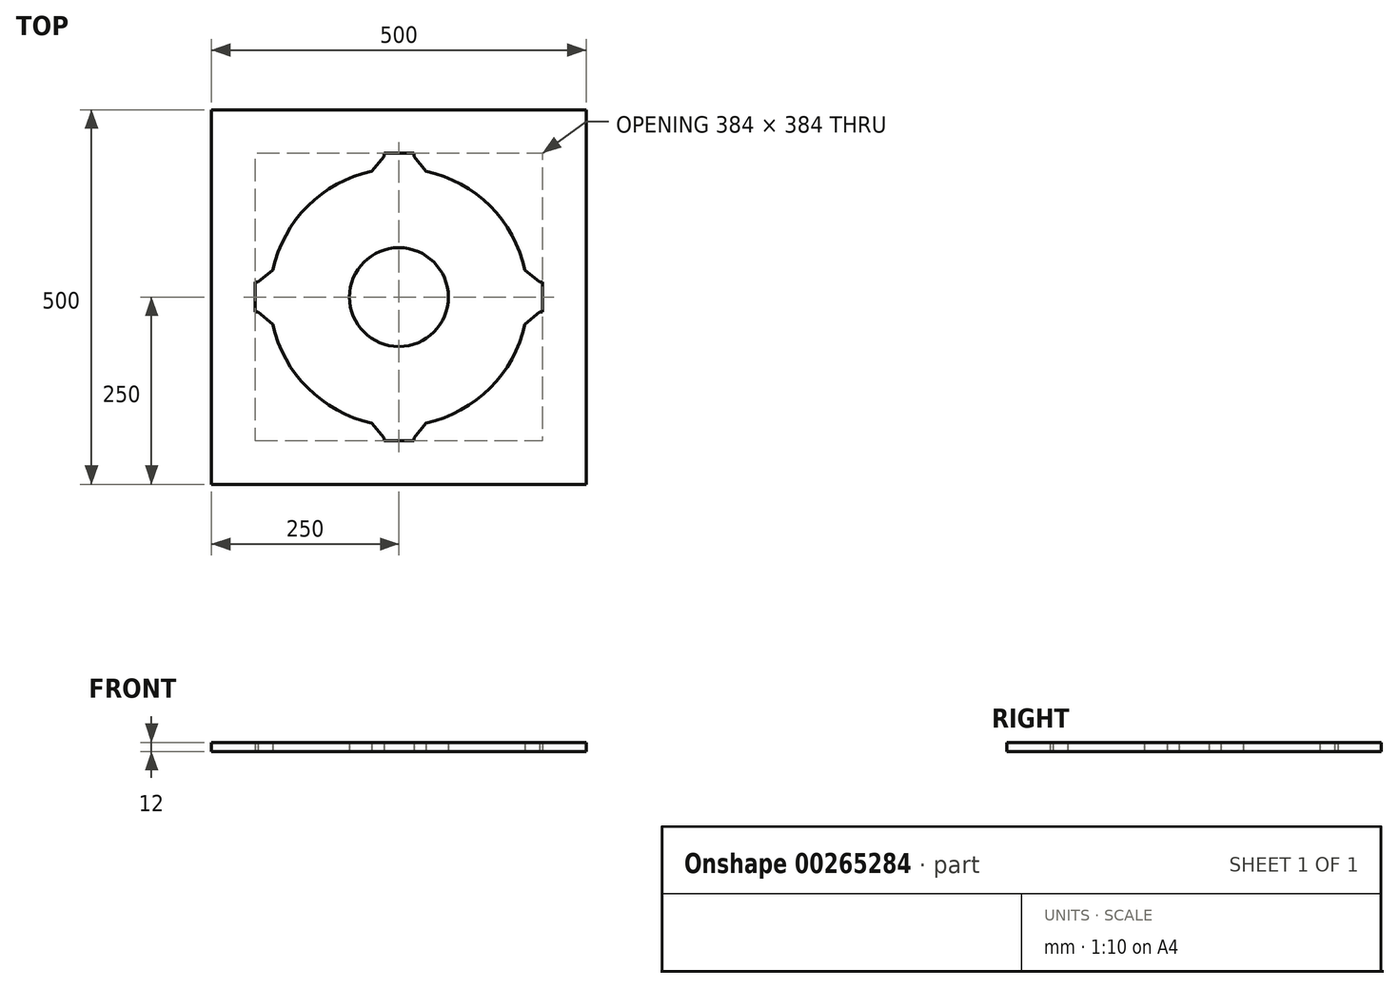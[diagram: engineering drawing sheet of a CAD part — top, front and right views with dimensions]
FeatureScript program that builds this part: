
annotation { "Feature Type Name" : "Feature", "Feature Type Description" : "" }
export const myFeature = defineFeature(function(context is Context, id is Id, definition is map)
    precondition{}
    {
        {
            var Q0;
            Q0=qCreatedBy(makeId("Top.planeOp"),FACE);
            var sketch = newSketch(context, id + "F0", { "sketchPlane" : qUnion([Q0])});
            skLineSegment(sketch, "E0.bottom", {"start": v(250, 250) * mm, "end": v(-250, 250) * mm});
            skLineSegment(sketch, "E0.top", {"start": v(250, -250) * mm, "end": v(-250, -250) * mm});
            skLineSegment(sketch, "E0.left", {"start": v(-250, -250) * mm, "end": v(-250, 250) * mm});
            skLineSegment(sketch, "E0.right", {"start": v(250, -250) * mm, "end": v(250, 250) * mm});
            skPoint(sketch, "E0.middle", {"position": v(0, 0) * mm});
            skSolve(sketch);
        }
        {
            var Q0;
            Q0 = qSketchRegion(id + "F0", true);
            extrude(context, id + "F1", {"entities" : qUnion([Q0]), "depth" : 12 * mm});
        }
        {
            var Q0;
            Q0=makeQuery(id+"F1.opExtrude","CAP_FACE",FACE,{"disambiguationData":[OSD([sQuery(id+"F0.wireOp",EDGE,"E0.bottom"),sQuery(id+"F0.wireOp",EDGE,"E0.top"),sQuery(id+"F0.wireOp",EDGE,"E0.left"),sQuery(id+"F0.wireOp",EDGE,"E0.right")])],"isStart":true});
            var sketch = newSketch(context, id + "F2", { "sketchPlane" : qUnion([Q0])});
            skCircle(sketch, "E1", {"center": v(0, 0) * mm, "radius": 172 * mm});
            skLineSegment(sketch, "E2", {"start": v(-172, 0) * mm, "end": v(172, 0) * mm, "construction": true});
            skLineSegment(sketch, "E3", {"start": v(0, -172) * mm, "end": v(0, 172) * mm, "construction": true});
            skLineSegment(sketch, "E4.bottom", {"start": v(-152, 20) * mm, "end": v(-192, 20) * mm});
            skLineSegment(sketch, "E4.top", {"start": v(-152, -20) * mm, "end": v(-192, -20) * mm});
            skLineSegment(sketch, "E4.left", {"start": v(-152, 20) * mm, "end": v(-152, -20) * mm, "construction": true});
            skLineSegment(sketch, "E4.right", {"start": v(-192, 20) * mm, "end": v(-192, -20) * mm});
            skPoint(sketch, "E4.middle", {"position": v(-172, 0) * mm});
            skLineSegment(sketch, "E5.bottom", {"start": v(20, -192) * mm, "end": v(-20, -192) * mm});
            skLineSegment(sketch, "E5.top", {"start": v(20, -152) * mm, "end": v(-20, -152) * mm, "construction": true});
            skLineSegment(sketch, "E5.left", {"start": v(20, -192) * mm, "end": v(20, -152) * mm});
            skLineSegment(sketch, "E5.right", {"start": v(-20, -192) * mm, "end": v(-20, -152) * mm});
            skPoint(sketch, "E5.middle", {"position": v(0, -172) * mm});
            skLineSegment(sketch, "E6.bottom", {"start": v(192, 20) * mm, "end": v(152, 20) * mm});
            skLineSegment(sketch, "E6.top", {"start": v(192, -20) * mm, "end": v(152, -20) * mm});
            skLineSegment(sketch, "E6.left", {"start": v(192, 20) * mm, "end": v(192, -20) * mm});
            skLineSegment(sketch, "E6.right", {"start": v(152, 20) * mm, "end": v(152, -20) * mm, "construction": true});
            skPoint(sketch, "E6.middle", {"position": v(172, 0) * mm});
            skLineSegment(sketch, "E7.bottom", {"start": v(20, 192) * mm, "end": v(-20, 192) * mm});
            skLineSegment(sketch, "E7.top", {"start": v(20, 152) * mm, "end": v(-20, 152) * mm, "construction": true});
            skLineSegment(sketch, "E7.left", {"start": v(20, 192) * mm, "end": v(20, 152) * mm});
            skLineSegment(sketch, "E7.right", {"start": v(-20, 192) * mm, "end": v(-20, 152) * mm});
            skPoint(sketch, "E7.middle", {"position": v(0, 172) * mm});
            skCircle(sketch, "E8", {"center": v(0, 0) * mm, "radius": 66 * mm});
            skSolve(sketch);
        }
        {
            var Q0;
            Q0 = qSketchRegion(id + "F2", true);
            extrude(context, id + "F3", {"entities" : qUnion([Q0]), "operationType" : NewBodyOperationType.REMOVE, "endBound" : BoundingType.UP_TO_NEXT, "oppositeDirection" : true, "depth" : 25.4 * mm});
        }
        {
            var Q0;
            Q0=makeQuery(id+"F3.boolean.opBoolean","COPY",EDGE,{"derivedFrom":makeQuery(id+"F3.opExtrude","SWEPT_EDGE",EDGE,{"disambiguationData":[OSD([sQuery(id+"F2.wireOp",EDGE,"E1"),sQuery(id+"F2.wireOp",EDGE,"E4.top")])]})});
            var Q1;
            Q1=makeQuery(id+"F3.boolean.opBoolean","COPY",EDGE,{"derivedFrom":makeQuery(id+"F3.opExtrude","SWEPT_EDGE",EDGE,{"disambiguationData":[OSD([sQuery(id+"F2.wireOp",EDGE,"E1"),sQuery(id+"F2.wireOp",EDGE,"E4.bottom")])]})});
            var Q2;
            Q2=makeQuery(id+"F3.boolean.opBoolean","COPY",EDGE,{"derivedFrom":makeQuery(id+"F3.opExtrude","SWEPT_EDGE",EDGE,{"disambiguationData":[OSD([sQuery(id+"F2.wireOp",EDGE,"E1"),sQuery(id+"F2.wireOp",EDGE,"E7.right")])]})});
            var Q3;
            Q3=makeQuery(id+"F3.boolean.opBoolean","COPY",EDGE,{"derivedFrom":makeQuery(id+"F3.opExtrude","SWEPT_EDGE",EDGE,{"disambiguationData":[OSD([sQuery(id+"F2.wireOp",EDGE,"E1"),sQuery(id+"F2.wireOp",EDGE,"E7.left")])]})});
            var Q4;
            Q4=makeQuery(id+"F3.boolean.opBoolean","COPY",EDGE,{"derivedFrom":makeQuery(id+"F3.opExtrude","SWEPT_EDGE",EDGE,{"disambiguationData":[OSD([sQuery(id+"F2.wireOp",EDGE,"E1"),sQuery(id+"F2.wireOp",EDGE,"E6.top")])]})});
            var Q5;
            Q5=makeQuery(id+"F3.boolean.opBoolean","COPY",EDGE,{"derivedFrom":makeQuery(id+"F3.opExtrude","SWEPT_EDGE",EDGE,{"disambiguationData":[OSD([sQuery(id+"F2.wireOp",EDGE,"E1"),sQuery(id+"F2.wireOp",EDGE,"E5.right")])]})});
            var Q6;
            Q6=makeQuery(id+"F3.boolean.opBoolean","COPY",EDGE,{"derivedFrom":makeQuery(id+"F3.opExtrude","SWEPT_EDGE",EDGE,{"disambiguationData":[OSD([sQuery(id+"F2.wireOp",EDGE,"E1"),sQuery(id+"F2.wireOp",EDGE,"E5.left")])]})});
            var Q7;
            Q7=makeQuery(id+"F3.boolean.opBoolean","COPY",EDGE,{"derivedFrom":makeQuery(id+"F3.opExtrude","SWEPT_EDGE",EDGE,{"disambiguationData":[OSD([sQuery(id+"F2.wireOp",EDGE,"E1"),sQuery(id+"F2.wireOp",EDGE,"E6.bottom")])]})});
            chamfer(context, id + "F4", {"entities" : qUnion([Q0, Q1, Q2, Q3, Q4, Q5, Q6, Q7]), "width" : 20.32 * mm, "tangentPropagation" : true});
        }
    });
